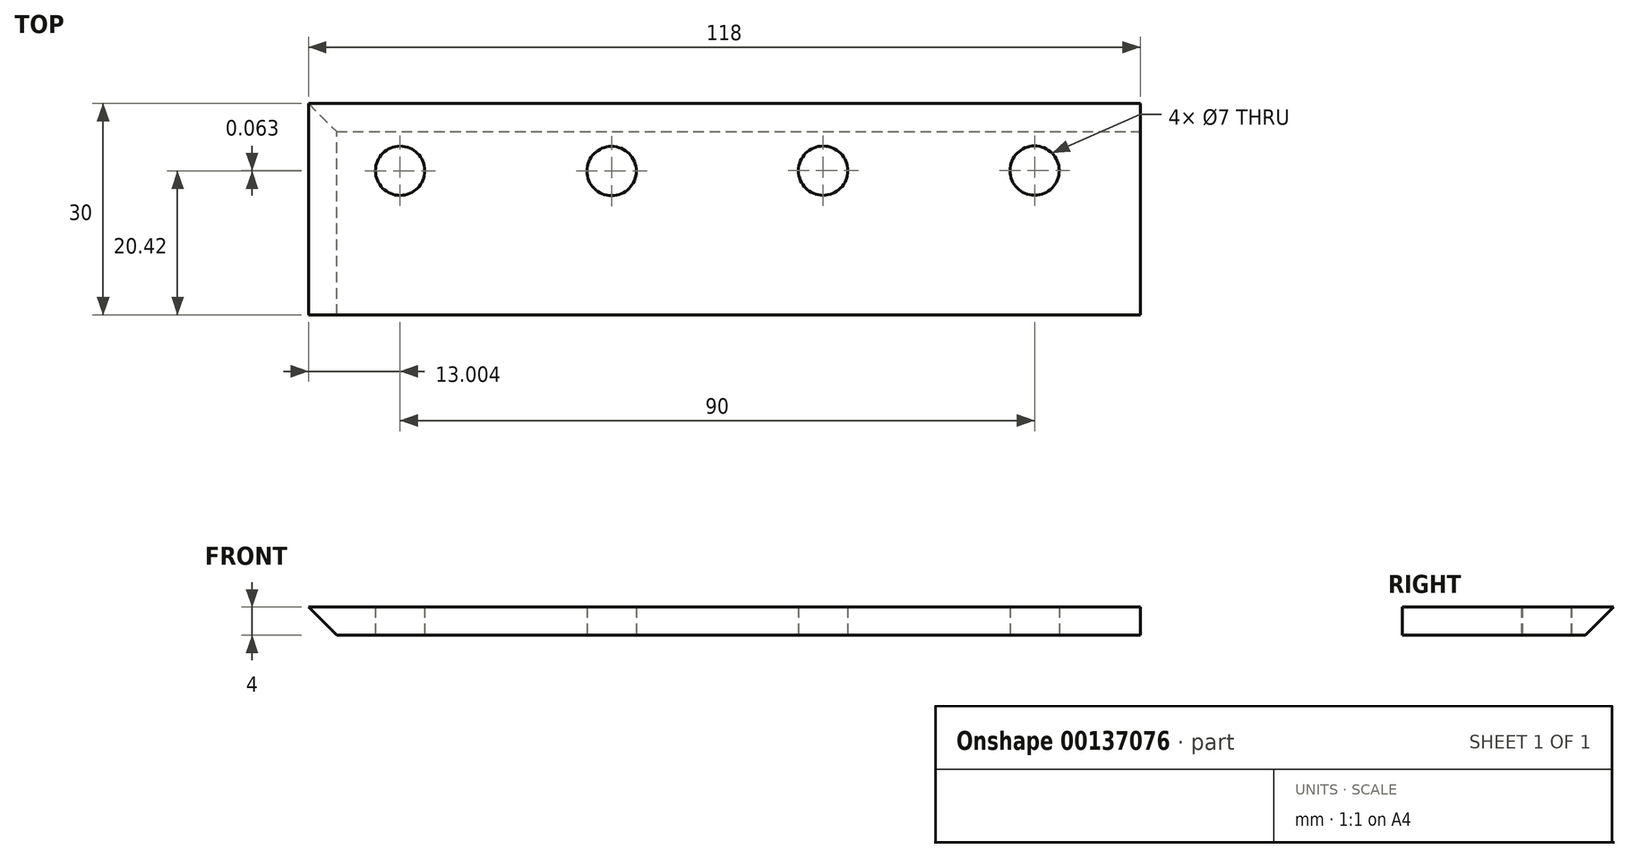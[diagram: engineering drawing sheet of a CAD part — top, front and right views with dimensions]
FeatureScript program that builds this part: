
annotation { "Feature Type Name" : "Feature", "Feature Type Description" : "" }
export const myFeature = defineFeature(function(context is Context, id is Id, definition is map)
    precondition{}
    {
        {
            var Q0;
            Q0=qCreatedBy(makeId("Top.planeOp"),FACE);
            var sketch = newSketch(context, id + "F0", { "sketchPlane" : qUnion([Q0])});
            skLineSegment(sketch, "E0", {"start": v(-71.75, 0.85) * mm, "end": v(-71.75, -29.15) * mm});
            skLineSegment(sketch, "E1", {"start": v(-71.75, -29.15) * mm, "end": v(46.25, -29.15) * mm});
            skLineSegment(sketch, "E2", {"start": v(46.25, -29.15) * mm, "end": v(46.25, 0.85) * mm});
            skCircle(sketch, "E3", {"center": v(-58.75, -8.69) * mm, "radius": 3.5 * mm});
            skCircle(sketch, "E4", {"center": v(-28.75, -8.73) * mm, "radius": 3.5 * mm});
            skCircle(sketch, "E5", {"center": v(1.25, -8.68) * mm, "radius": 3.5 * mm});
            skCircle(sketch, "E6", {"center": v(31.25, -8.67) * mm, "radius": 3.5 * mm});
            skLineSegment(sketch, "E7", {"start": v(-71.75, 0.85) * mm, "end": v(-71.75, -3.15) * mm});
            skLineSegment(sketch, "E8", {"start": v(-71.75, -3.15) * mm, "end": v(-71.75, -5.15) * mm});
            skLineSegment(sketch, "E9", {"start": v(-58.75, 0.85) * mm, "end": v(-58.75, -29.15) * mm});
            skLineSegment(sketch, "E10", {"start": v(46.25, 0.85) * mm, "end": v(-58.75, 0.85) * mm});
            skLineSegment(sketch, "E11", {"start": v(-71.75, 0.85) * mm, "end": v(-58.75, 0.85) * mm});
            skSolve(sketch);
        }
        {
            var Q0;
            Q0=qSketchRegion(id+"F0",true);
            extrude(context, id + "F1", {"entities" : qUnion([Q0]), "depth" : 4 * mm});
        }
        {
            var Q0;
            Q0=makeQuery(id+"F1.opExtrude","CAP_EDGE",EDGE,{"disambiguationData":[OSD([sQuery(id+"F0.wireOp",EDGE,"E0"),sQuery(id+"F0.wireOp",EDGE,"E7"),sQuery(id+"F0.wireOp",EDGE,"E8")])],"isStart":true});
            var Q1;
            Q1=makeQuery(id+"F1.opExtrude","CAP_EDGE",EDGE,{"disambiguationData":[OSD([sQuery(id+"F0.wireOp",EDGE,"E10"),sQuery(id+"F0.wireOp",EDGE,"E11")])],"isStart":true});
            chamfer(context, id + "F2", {"entities" : qUnion([Q0, Q1]), "width" : 4 * mm, "tangentPropagation" : true});
        }
    });
